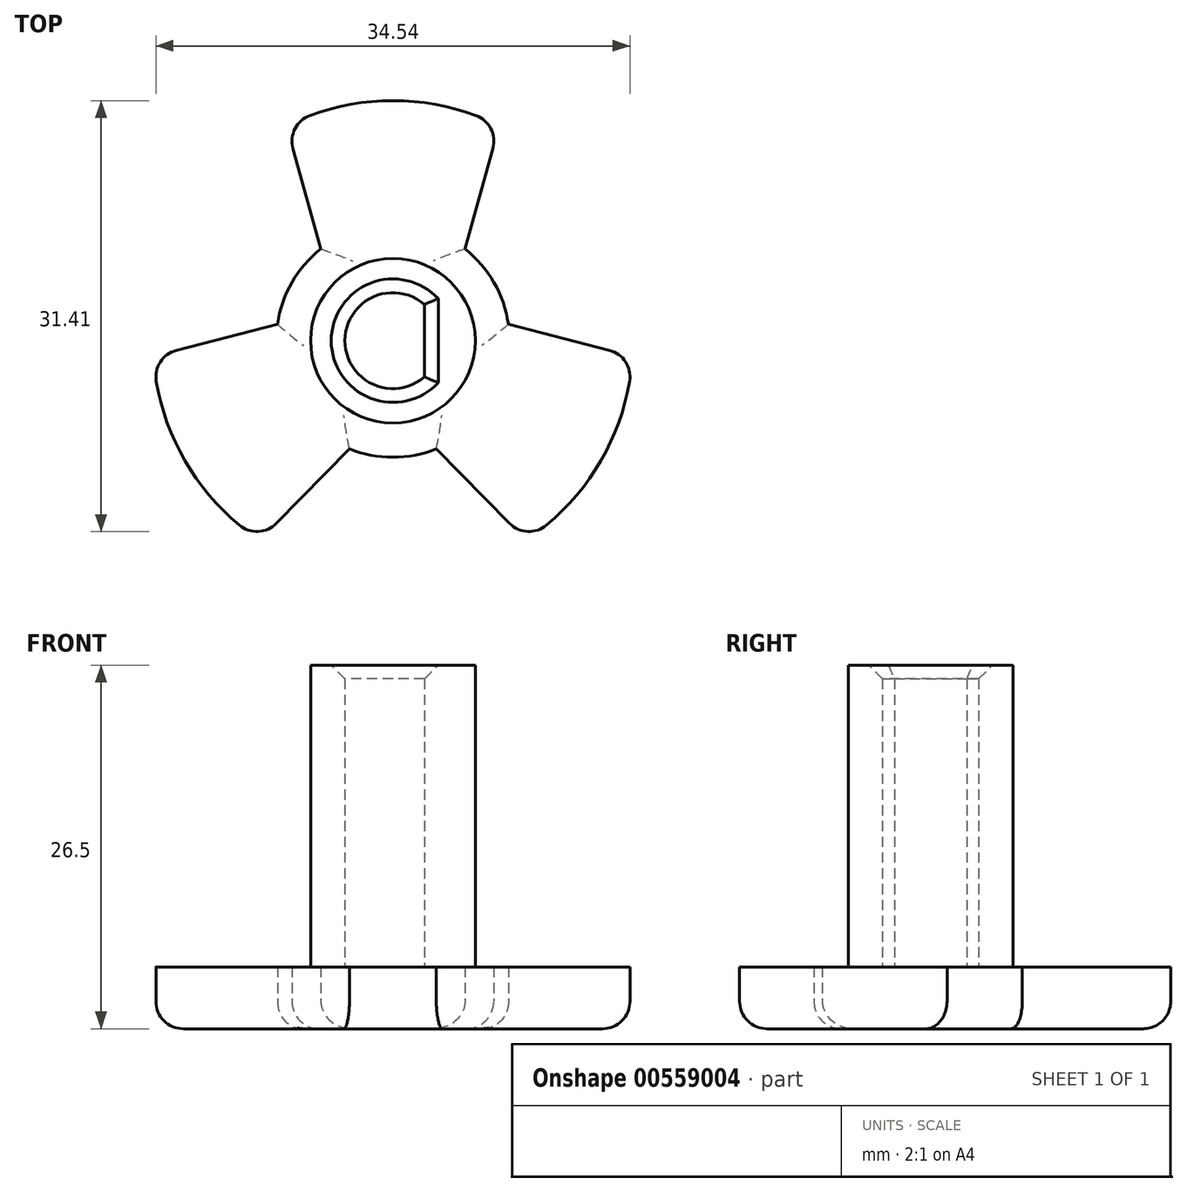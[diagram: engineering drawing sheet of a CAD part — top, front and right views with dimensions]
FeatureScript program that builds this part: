
annotation { "Feature Type Name" : "Feature", "Feature Type Description" : "" }
export const myFeature = defineFeature(function(context is Context, id is Id, definition is map)
    precondition{}
    {
        {
            var Q0;
            Q0=qCreatedBy(makeId("Top.planeOp"),FACE);
            var sketch = newSketch(context, id + "F0", { "sketchPlane" : qUnion([Q0])});
            skArc(sketch, "E0", {"start": v(-3.16, -7.89) * mm, "mid": v(0, -8.5) * mm, "end": v(3.16, -7.89) * mm});
            skArc(sketch, "E1", {"start": v(-17.25, -2.97) * mm, "mid": v(-15.16, -8.75) * mm, "end": v(-11.2, -13.45) * mm});
            skLineSegment(sketch, "E2", {"start": v(-7.28, 14.01) * mm, "end": v(-5.25, 6.68) * mm});
            skLineSegment(sketch, "E3", {"start": v(7.28, 14.01) * mm, "end": v(5.25, 6.68) * mm});
            skLineSegment(sketch, "E4.1.0", {"start": v(-15.77, -0.7) * mm, "end": v(-8.41, 1.2) * mm});
            skLineSegment(sketch, "E4.1.1", {"start": v(-8.5, -13.31) * mm, "end": v(-3.16, -7.89) * mm});
            skLineSegment(sketch, "E4.2.0", {"start": v(8.5, -13.31) * mm, "end": v(3.16, -7.89) * mm});
            skLineSegment(sketch, "E4.2.1", {"start": v(15.77, -0.7) * mm, "end": v(8.41, 1.2) * mm});
            skArc(sketch, "E5.trimOffspring", {"start": v(6.05, 16.42) * mm, "mid": v(0, 17.5) * mm, "end": v(-6.05, 16.42) * mm});
            skArc(sketch, "E6.trimOffspring", {"start": v(11.2, -13.45) * mm, "mid": v(15.16, -8.75) * mm, "end": v(17.25, -2.97) * mm});
            skPoint(sketch, "E7.visualSharp", {"position": v(-17.46, -1.13) * mm});
            skArc(sketch, "E7.filletArc", {"start": v(-15.77, -0.7) * mm, "mid": v(-16.95, -1.55) * mm, "end": v(-17.25, -2.97) * mm});
            skPoint(sketch, "E8.visualSharp", {"position": v(-9.71, -14.56) * mm});
            skArc(sketch, "E8.filletArc", {"start": v(-11.2, -13.45) * mm, "mid": v(-9.82, -13.9) * mm, "end": v(-8.5, -13.31) * mm});
            skPoint(sketch, "E9.visualSharp", {"position": v(9.71, -14.56) * mm});
            skArc(sketch, "E9.filletArc", {"start": v(8.5, -13.31) * mm, "mid": v(9.82, -13.9) * mm, "end": v(11.2, -13.45) * mm});
            skPoint(sketch, "E10.visualSharp", {"position": v(17.46, -1.13) * mm});
            skArc(sketch, "E10.filletArc", {"start": v(17.25, -2.97) * mm, "mid": v(16.95, -1.55) * mm, "end": v(15.77, -0.7) * mm});
            skPoint(sketch, "E11.visualSharp", {"position": v(7.75, 15.7) * mm});
            skArc(sketch, "E11.filletArc", {"start": v(7.28, 14.01) * mm, "mid": v(7.14, 15.46) * mm, "end": v(6.05, 16.42) * mm});
            skPoint(sketch, "E12.visualSharp", {"position": v(-7.75, 15.7) * mm});
            skArc(sketch, "E12.filletArc", {"start": v(-6.05, 16.42) * mm, "mid": v(-7.14, 15.46) * mm, "end": v(-7.28, 14.01) * mm});
            skArc(sketch, "E13.trimOffspring", {"start": v(-5.25, 6.68) * mm, "mid": v(-7.36, 4.25) * mm, "end": v(-8.41, 1.2) * mm});
            skArc(sketch, "E14.trimOffspring", {"start": v(8.41, 1.2) * mm, "mid": v(7.36, 4.25) * mm, "end": v(5.25, 6.68) * mm});
            skSolve(sketch);
        }
        {
            var Q0;
            Q0=makeQuery(id+"F0.imprint","IMPRINT",FACE,{"disambiguationData":[TD([[makeQuery(id+"F0.imprint","IMPRINT",EDGE,{"derivedFrom":sQuery(id+"F0.wireOp",EDGE,"E0")}),1.0]])]});
            extrude(context, id + "F1", {"entities" : qUnion([Q0]), "depth" : 4.5 * mm, "offsetDistance" : 25 * mm});
        }
        {
            var Q0;
            Q0=makeQuery(id+"F1.opExtrude","CAP_FACE",FACE,{"disambiguationData":[OSD([sQuery(id+"F0.wireOp",EDGE,"E0"),sQuery(id+"F0.wireOp",EDGE,"E1"),sQuery(id+"F0.wireOp",EDGE,"E2"),sQuery(id+"F0.wireOp",EDGE,"E3"),sQuery(id+"F0.wireOp",EDGE,"E4.1.0"),sQuery(id+"F0.wireOp",EDGE,"E4.1.1"),sQuery(id+"F0.wireOp",EDGE,"E4.2.0"),sQuery(id+"F0.wireOp",EDGE,"E4.2.1"),sQuery(id+"F0.wireOp",EDGE,"E5.trimOffspring"),sQuery(id+"F0.wireOp",EDGE,"E6.trimOffspring"),sQuery(id+"F0.wireOp",EDGE,"E7.filletArc"),sQuery(id+"F0.wireOp",EDGE,"E8.filletArc"),sQuery(id+"F0.wireOp",EDGE,"E9.filletArc"),sQuery(id+"F0.wireOp",EDGE,"E10.filletArc"),sQuery(id+"F0.wireOp",EDGE,"E11.filletArc"),sQuery(id+"F0.wireOp",EDGE,"E12.filletArc"),sQuery(id+"F0.wireOp",EDGE,"E13.trimOffspring"),sQuery(id+"F0.wireOp",EDGE,"E14.trimOffspring")])],"isStart":false});
            var sketch = newSketch(context, id + "F2", { "sketchPlane" : qUnion([Q0])});
            skCircle(sketch, "E15", {"center": v(0, 0) * mm, "radius": 6 * mm});
            skArc(sketch, "E16", {"start": v(2.3, 2.64) * mm, "mid": v(-3.5, 0) * mm, "end": v(2.3, -2.64) * mm});
            skLineSegment(sketch, "E17", {"start": v(2.3, 2.64) * mm, "end": v(2.3, -2.64) * mm});
            skPoint(sketch, "E18", {"position": v(-3.5, 0) * mm});
            skSolve(sketch);
        }
        {
            var Q0;
            Q0=makeQuery(id+"F2.imprint","IMPRINT",FACE,{"disambiguationData":[TD([[makeQuery(id+"F2.imprint","IMPRINT",EDGE,{"derivedFrom":sQuery(id+"F2.wireOp",EDGE,"E15")}),1.0]])]});
            extrude(context, id + "F3", {"entities" : qUnion([Q0]), "operationType" : NewBodyOperationType.ADD, "depth" : 22 * mm, "offsetDistance" : 25 * mm});
        }
        {
            var Q0;
            Q0=makeQuery(id+"F1.opExtrude","CAP_EDGE",EDGE,{"disambiguationData":[OSD([sQuery(id+"F0.wireOp",EDGE,"E2")])],"isStart":true});
            var Q1;
            Q1=makeQuery(id+"F1.opExtrude","CAP_EDGE",EDGE,{"disambiguationData":[OSD([sQuery(id+"F0.wireOp",EDGE,"E4.1.0")])],"isStart":true});
            var Q2;
            Q2=makeQuery(id+"F1.opExtrude","CAP_EDGE",EDGE,{"disambiguationData":[OSD([sQuery(id+"F0.wireOp",EDGE,"E6.trimOffspring")])],"isStart":true});
            var Q3;
            Q3=makeQuery(id+"F1.opExtrude","CAP_EDGE",EDGE,{"disambiguationData":[OSD([sQuery(id+"F0.wireOp",EDGE,"E14.trimOffspring")])],"isStart":true});
            var Q4;
            Q4=makeQuery(id+"F1.opExtrude","CAP_EDGE",EDGE,{"disambiguationData":[OSD([sQuery(id+"F0.wireOp",EDGE,"E0")])],"isStart":true});
            var Q5;
            Q5=makeQuery(id+"F1.opExtrude","CAP_EDGE",EDGE,{"disambiguationData":[OSD([sQuery(id+"F0.wireOp",EDGE,"E13.trimOffspring")])],"isStart":true});
            fillet(context, id + "F4", {"entities" : qUnion([Q0, Q1, Q2, Q3, Q4, Q5]), "radius" : 2 * mm, "tangentPropagation" : true, "allowEdgeOverflow" : false});
        }
        {
            var Q0;
            Q0=makeQuery(id+"F3.opExtrude","CAP_EDGE",EDGE,{"disambiguationData":[OSD([sQuery(id+"F2.wireOp",EDGE,"E16")])],"isStart":false});
            var Q1;
            Q1=makeQuery(id+"F3.opExtrude","CAP_EDGE",EDGE,{"disambiguationData":[OSD([sQuery(id+"F2.wireOp",EDGE,"E17")])],"isStart":false});
            chamfer(context, id + "F5", {"entities" : qUnion([Q0, Q1]), "width" : 1 * mm, "tangentPropagation" : true});
        }
    });
